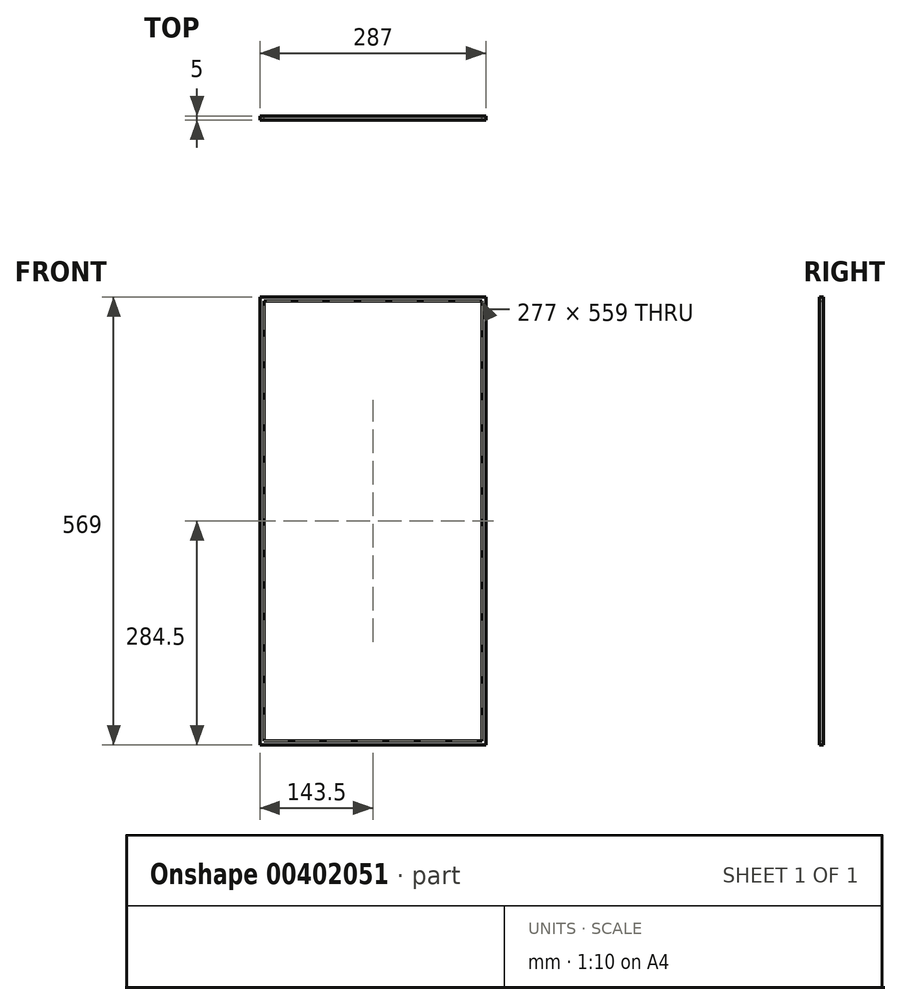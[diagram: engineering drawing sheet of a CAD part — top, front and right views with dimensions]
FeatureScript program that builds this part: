
annotation { "Feature Type Name" : "Feature", "Feature Type Description" : "" }
export const myFeature = defineFeature(function(context is Context, id is Id, definition is map)
    precondition{}
    {
        {
            var Q0;
            Q0=qCreatedBy(makeId("Front.planeOp"),FACE);
            var sketch = newSketch(context, id + "F0", { "sketchPlane" : qUnion([Q0])});
            skPoint(sketch, "E0.middle", {"position": v(0, 0) * mm});
            skLineSegment(sketch, "E1.bottom", {"start": v(138.5, 279.5) * mm, "end": v(-138.5, 279.5) * mm});
            skLineSegment(sketch, "E1.top", {"start": v(138.5, 284.5) * mm, "end": v(-138.5, 284.5) * mm});
            skLineSegment(sketch, "E1.left", {"start": v(138.5, 279.5) * mm, "end": v(138.5, 284.5) * mm});
            skLineSegment(sketch, "E1.right", {"start": v(-138.5, 279.5) * mm, "end": v(-138.5, 284.5) * mm});
            skLineSegment(sketch, "E2.bottom", {"start": v(138.5, 284.5) * mm, "end": v(143.5, 284.5) * mm});
            skLineSegment(sketch, "E2.top", {"start": v(138.5, -284.5) * mm, "end": v(143.5, -284.5) * mm});
            skLineSegment(sketch, "E2.left", {"start": v(138.5, 284.5) * mm, "end": v(138.5, -284.5) * mm});
            skLineSegment(sketch, "E2.right", {"start": v(143.5, 284.5) * mm, "end": v(143.5, -284.5) * mm});
            skLineSegment(sketch, "E3.MirrorCS", {"start": v(-138.5, -284.5) * mm, "end": v(-143.5, -284.5) * mm});
            skLineSegment(sketch, "E4.MirrorCS", {"start": v(-138.5, 284.5) * mm, "end": v(-138.5, -284.5) * mm});
            skLineSegment(sketch, "E5.MirrorCS", {"start": v(-138.5, 284.5) * mm, "end": v(-143.5, 284.5) * mm});
            skLineSegment(sketch, "E6.MirrorCS", {"start": v(-143.5, 284.5) * mm, "end": v(-143.5, -284.5) * mm});
            skLineSegment(sketch, "E7.MirrorCS", {"start": v(138.5, -279.5) * mm, "end": v(-138.5, -279.5) * mm});
            skLineSegment(sketch, "E8.MirrorCS", {"start": v(138.5, -284.5) * mm, "end": v(-138.5, -284.5) * mm});
            skSolve(sketch);
        }
        {
            var Q0;
            {var subQ1=sQuery(id+"F0.wireOp",EDGE,"E3.MirrorCS");Q0=makeQuery(id+"F0.imprint","IMPRINT",FACE,{"disambiguationData":[TD([[makeQuery(id+"F0.imprint","IMPRINT",EDGE,{"derivedFrom":subQ1}),-1.0]])]});}
            var Q1;
            {var subQ0=sQuery(id+"F0.wireOp",EDGE,"E1.bottom");Q1=makeQuery(id+"F0.imprint","IMPRINT",FACE,{"disambiguationData":[TD([[makeQuery(id+"F0.imprint","IMPRINT",EDGE,{"derivedFrom":subQ0}),-1.0]])]});}
            var Q2;
            {var subQ3=sQuery(id+"F0.wireOp",EDGE,"E2.bottom");Q2=makeQuery(id+"F0.imprint","IMPRINT",FACE,{"disambiguationData":[TD([[makeQuery(id+"F0.imprint","IMPRINT",EDGE,{"derivedFrom":subQ3}),-1.0]])]});}
            var Q3;
            {var subQ2=sQuery(id+"F0.wireOp",EDGE,"E7.MirrorCS");Q3=makeQuery(id+"F0.imprint","IMPRINT",FACE,{"disambiguationData":[TD([[makeQuery(id+"F0.imprint","IMPRINT",EDGE,{"derivedFrom":subQ2}),1.0]])]});}
            extrude(context, id + "F1", {"entities" : qUnion([Q0, Q1, Q2, Q3]), "depth" : 5 * mm});
        }
    });
